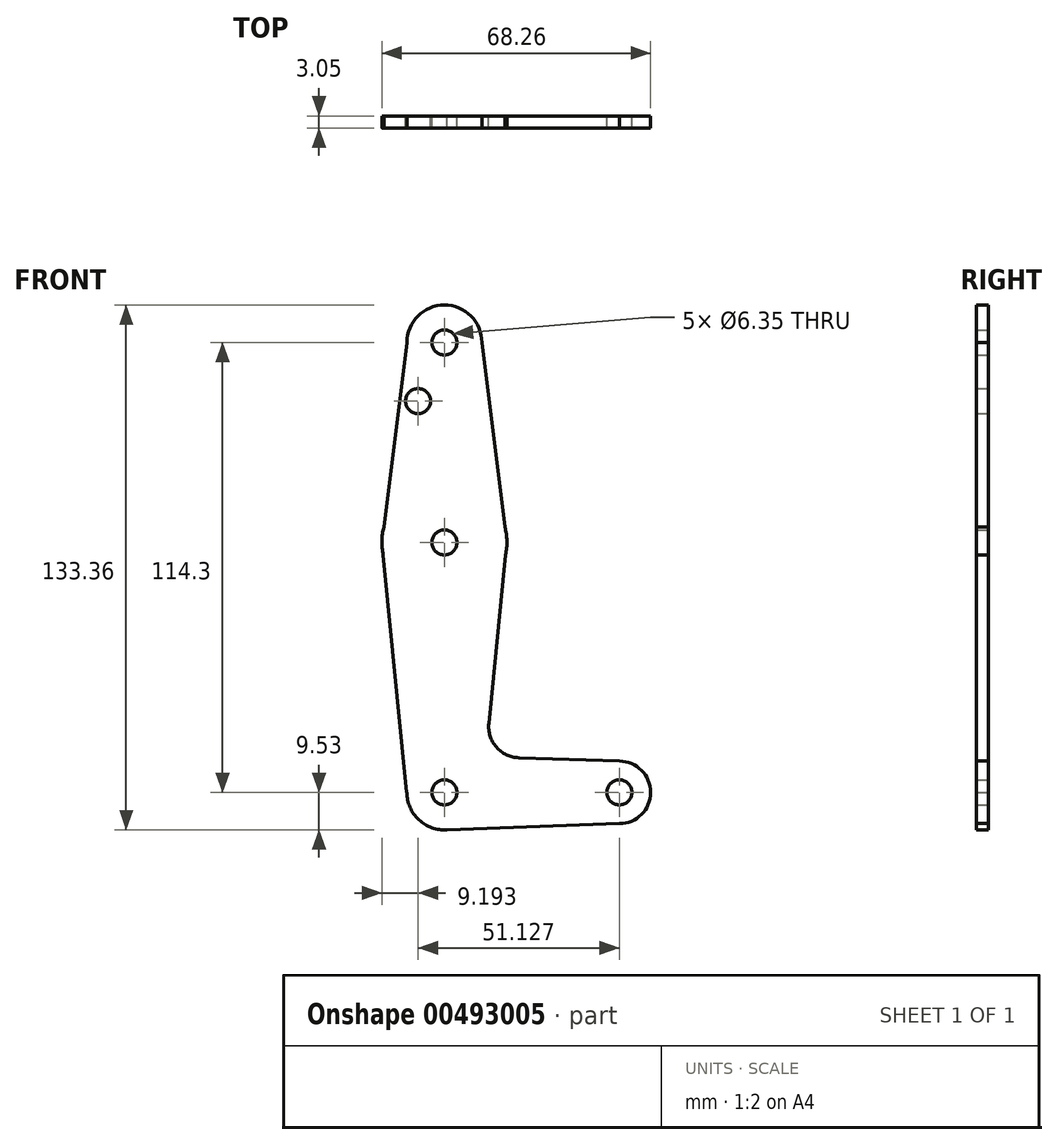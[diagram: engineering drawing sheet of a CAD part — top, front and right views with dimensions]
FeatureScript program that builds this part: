
annotation { "Feature Type Name" : "Feature", "Feature Type Description" : "" }
export const myFeature = defineFeature(function(context is Context, id is Id, definition is map)
    precondition{}
    {
        {
            var Q0;
            Q0=qCreatedBy(makeId("Front.planeOp"),FACE);
            var sketch = newSketch(context, id + "F0", { "sketchPlane" : qUnion([Q0])});
            skLineSegment(sketch, "E0", {"start": v(0, 0) * mm, "end": v(0, 114.3) * mm, "construction": true});
            skLineSegment(sketch, "E1", {"start": v(0, 0) * mm, "end": v(44.45, 0) * mm});
            skCircle(sketch, "E2", {"center": v(0, 114.3) * mm, "radius": 9.53 * mm});
            skCircle(sketch, "E3", {"center": v(0, 63.5) * mm, "radius": 15.88 * mm});
            skCircle(sketch, "E4", {"center": v(0, 0) * mm, "radius": 9.53 * mm});
            skCircle(sketch, "E5", {"center": v(44.45, 0) * mm, "radius": 7.94 * mm});
            skLineSegment(sketch, "E6", {"start": v(9.52, 114.3) * mm, "end": v(15.88, 63.5) * mm});
            skLineSegment(sketch, "E7", {"start": v(15.88, 63.5) * mm, "end": v(11.28, 17.54) * mm});
            skLineSegment(sketch, "E8", {"start": v(-9.52, 114.3) * mm, "end": v(-15.88, 63.5) * mm});
            skLineSegment(sketch, "E9", {"start": v(-15.88, 63.5) * mm, "end": v(-9.57, 0) * mm});
            skLineSegment(sketch, "E10", {"start": v(-9.57, 0) * mm, "end": v(9.53, 0) * mm});
            skLineSegment(sketch, "E11", {"start": v(0, -9.53) * mm, "end": v(44.45, -7.94) * mm});
            skLineSegment(sketch, "E12", {"start": v(0, 0) * mm, "end": v(-0.94, 9.48) * mm});
            skLineSegment(sketch, "E13", {"start": v(18.92, 8.8) * mm, "end": v(44.45, 7.94) * mm});
            skCircle(sketch, "E14", {"center": v(0, 114.3) * mm, "radius": 3.18 * mm});
            skCircle(sketch, "E15", {"center": v(0, 63.5) * mm, "radius": 3.18 * mm});
            skCircle(sketch, "E16", {"center": v(0, 0) * mm, "radius": 3.18 * mm});
            skCircle(sketch, "E17", {"center": v(44.45, 0) * mm, "radius": 3.18 * mm});
            skCircle(sketch, "E18", {"center": v(-6.68, 99.4) * mm, "radius": 3.18 * mm});
            skArc(sketch, "E19.filletArc", {"start": v(11.28, 17.54) * mm, "mid": v(13.2, 11.52) * mm, "end": v(18.92, 8.8) * mm});
            skSolve(sketch);
        }
        {
            var Q0;
            Q0 = qSketchRegion(id + "F0", true);
            var Q1;
            {var subQ1=sQuery(id+"F0.wireOp",EDGE,"E4");var subQ3=sQuery(id+"F0.wireOp",EDGE,"E12");var subQ4=makeQuery(id+"F0.imprint","INTERSECT",VERTEX,{"derivedFrom":[subQ1,subQ3]});Q1=makeQuery(id+"F0.imprint","IMPRINT",FACE,{"disambiguationData":[TD([[makeQuery(id+"F0.imprint","IMPRINT",EDGE,{"disambiguationData":[TD([[subQ4,1.0]])],"derivedFrom":subQ3}),-1.0]])]});}
            extrude(context, id + "F1", {"entities" : qUnion([Q0, Q1]), "depth" : 3.05 * mm});
        }
    });
